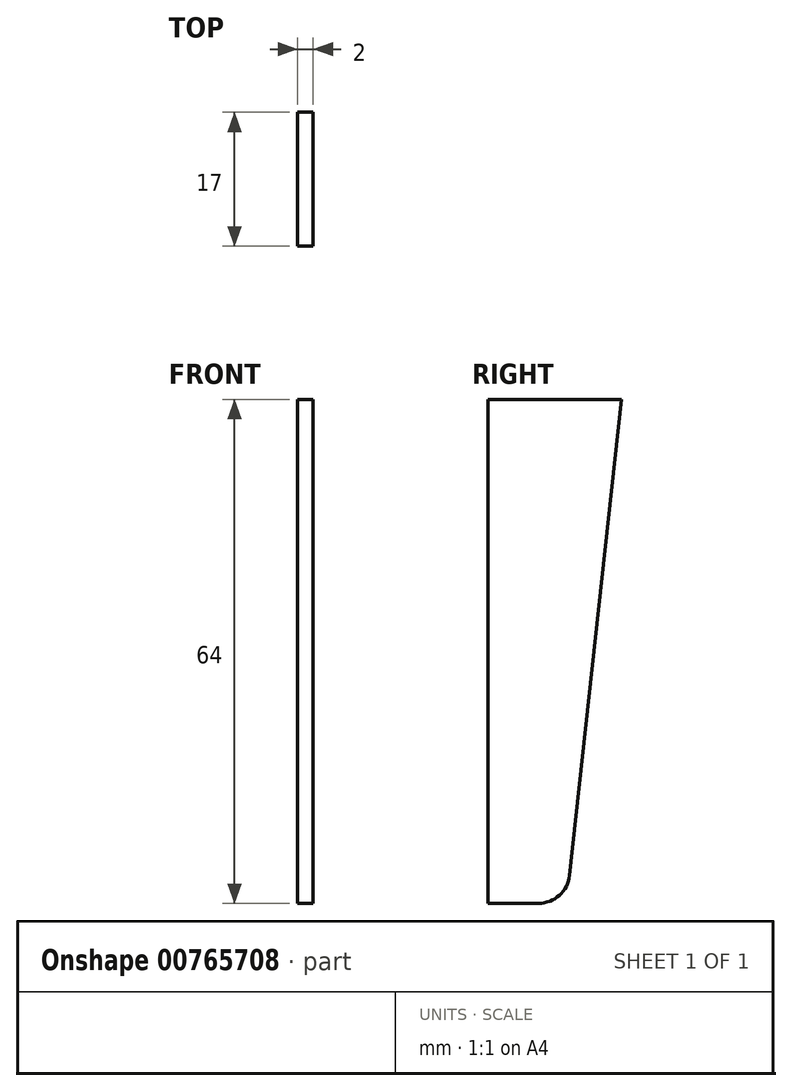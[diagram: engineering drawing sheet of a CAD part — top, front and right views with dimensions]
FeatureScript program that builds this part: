
annotation { "Feature Type Name" : "Feature", "Feature Type Description" : "" }
export const myFeature = defineFeature(function(context is Context, id is Id, definition is map)
    precondition{}
    {
        {
            var Q0;
            Q0=qCreatedBy(makeId("Right.planeOp"),FACE);
            var sketch = newSketch(context, id + "F0", { "sketchPlane" : qUnion([Q0])});
            skLineSegment(sketch, "E0", {"start": v(-48.58, 42.2) * mm, "end": v(-48.58, -21.8) * mm});
            skLineSegment(sketch, "E1", {"start": v(-48.58, 42.2) * mm, "end": v(-31.58, 42.2) * mm});
            skLineSegment(sketch, "E2", {"start": v(-48.58, -21.8) * mm, "end": v(-42.17, -21.8) * mm});
            skLineSegment(sketch, "E3", {"start": v(-38.2, -18.24) * mm, "end": v(-31.58, 42.2) * mm});
            skPoint(sketch, "E4.visualSharp", {"position": v(-38.58, -21.8) * mm});
            skArc(sketch, "E4.filletArc", {"start": v(-42.17, -21.8) * mm, "mid": v(-39.5, -20.78) * mm, "end": v(-38.2, -18.24) * mm});
            skSolve(sketch);
        }
        {
            var Q0;
            Q0=makeQuery(id+"F0.imprint","IMPRINT",FACE,{"disambiguationData":[TD([[makeQuery(id+"F0.imprint","IMPRINT",EDGE,{"derivedFrom":sQuery(id+"F0.wireOp",EDGE,"E0")}),1.0]])]});
            extrude(context, id + "F1", {"entities" : qUnion([Q0]), "depth" : 2 * mm, "offsetDistance" : 25 * mm});
        }
    });
